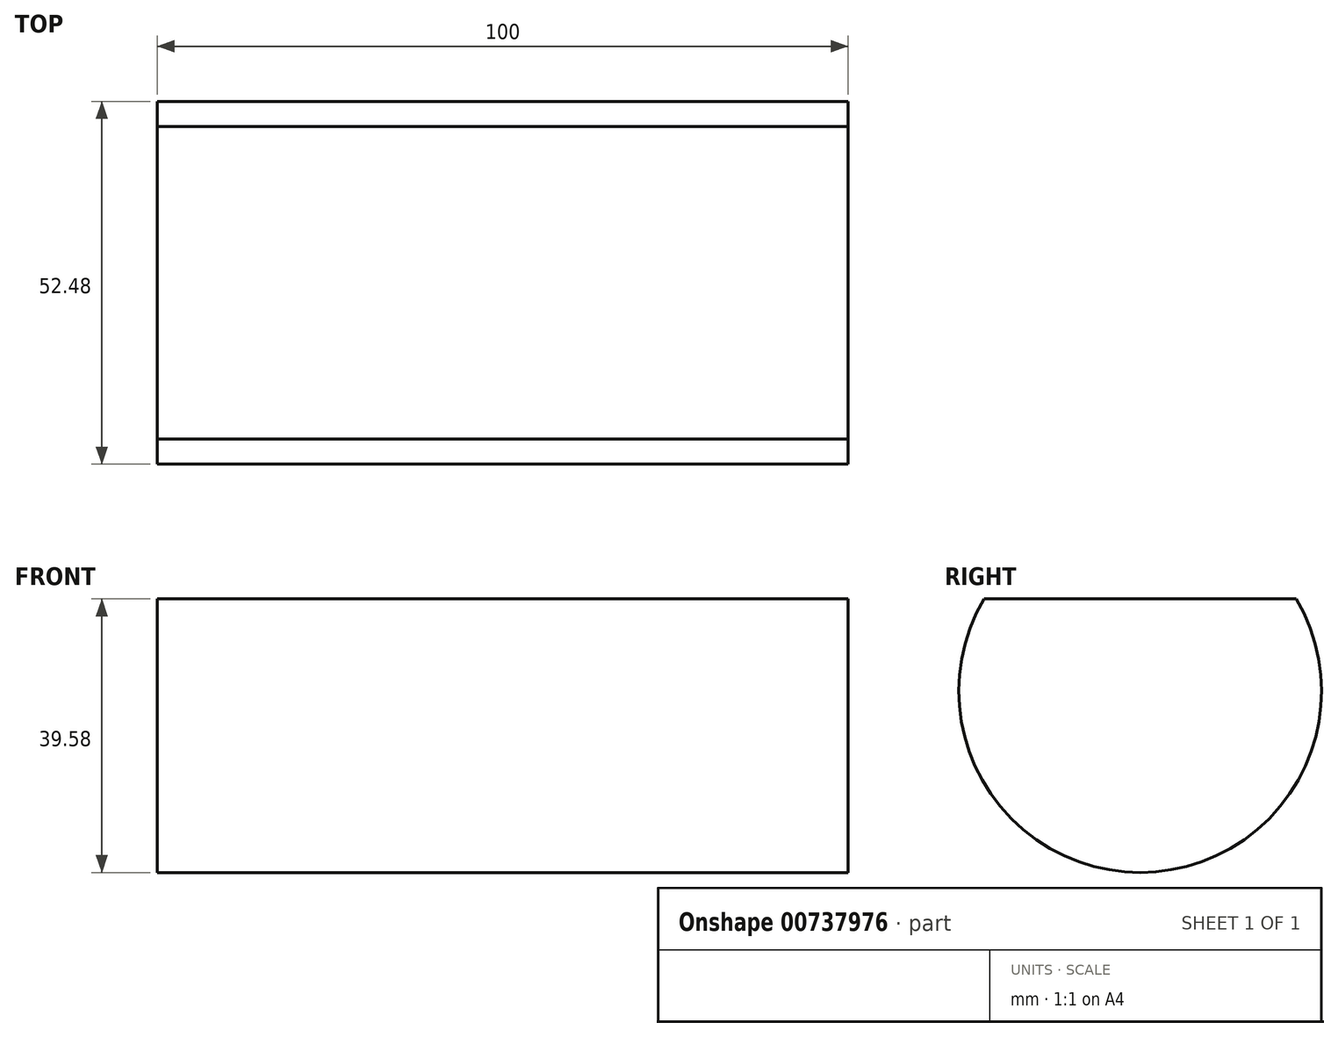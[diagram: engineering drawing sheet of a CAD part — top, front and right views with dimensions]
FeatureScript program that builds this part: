
annotation { "Feature Type Name" : "Feature", "Feature Type Description" : "" }
export const myFeature = defineFeature(function(context is Context, id is Id, definition is map)
    precondition{}
    {
        {
            var Q0;
            Q0=qCreatedBy(makeId("Right.planeOp"),FACE);
            var sketch = newSketch(context, id + "F0", { "sketchPlane" : qUnion([Q0])});
            skCircle(sketch, "E0", {"center": v(0, 0) * mm, "radius": 26.24 * mm});
            skSolve(sketch);
        }
        {
            var Q0;
            Q0=makeQuery(id+"F0.imprint","IMPRINT",FACE,{"disambiguationData":[TD([[makeQuery(id+"F0.imprint","IMPRINT",EDGE,{"derivedFrom":sQuery(id+"F0.wireOp",EDGE,"E0")}),1.0]])]});
            extrude(context, id + "F1", {"entities" : qUnion([Q0]), "depth" : 100 * mm, "offsetDistance" : 25 * mm});
        }
        {
            var Q0;
            Q0=qCreatedBy(makeId("Right.planeOp"),FACE);
            var sketch = newSketch(context, id + "F2", { "sketchPlane" : qUnion([Q0])});
            skLineSegment(sketch, "E1.bottom", {"start": v(-31.84, 34.57) * mm, "end": v(35.11, 34.57) * mm});
            skLineSegment(sketch, "E1.top", {"start": v(-31.84, 13.34) * mm, "end": v(35.11, 13.34) * mm});
            skLineSegment(sketch, "E1.left", {"start": v(-31.84, 34.57) * mm, "end": v(-31.84, 13.34) * mm});
            skLineSegment(sketch, "E1.right", {"start": v(35.11, 34.57) * mm, "end": v(35.11, 13.34) * mm});
            skSolve(sketch);
        }
        {
            var Q0;
            Q0=makeQuery(id+"F2.imprint","IMPRINT",FACE,{"disambiguationData":[TD([[makeQuery(id+"F2.imprint","IMPRINT",EDGE,{"derivedFrom":sQuery(id+"F2.wireOp",EDGE,"E1.bottom")}),-1.0]])]});
            extrude(context, id + "F3", {"entities" : qUnion([Q0]), "operationType" : NewBodyOperationType.REMOVE, "depth" : 100 * mm, "offsetDistance" : 25 * mm});
        }
    });
